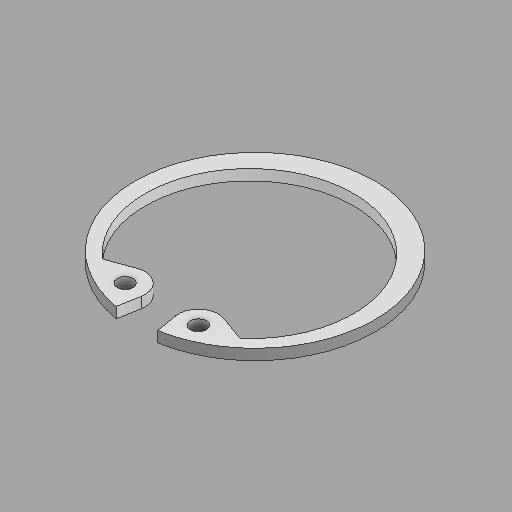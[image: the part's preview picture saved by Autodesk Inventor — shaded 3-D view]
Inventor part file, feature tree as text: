
AUTODESK INVENTOR PART (.ipt)
format: ipt  version: 2024.2 (Build 282272000, 272)  size: 104,448 bytes
history: native  units: in
note: dims shown in document units (in); Inventor stores cm internally (conversion verified against a paired STEP export)
features: fillet x1
ambient origin geometry x8: Origin, YZ Plane, XZ Plane, XY Plane, X Axis, Y Axis, Z Axis, Center Point
bodies: Solid1 (feature_tree)
feature tree (1):
  fillet  "Fillet1"  [1 undecoded]
note: 1 required parameter value undecoded (feature->parameter linkage not recoverable at this tier; creation-order binding heuristic only, values carry confidence <= 0.55)
